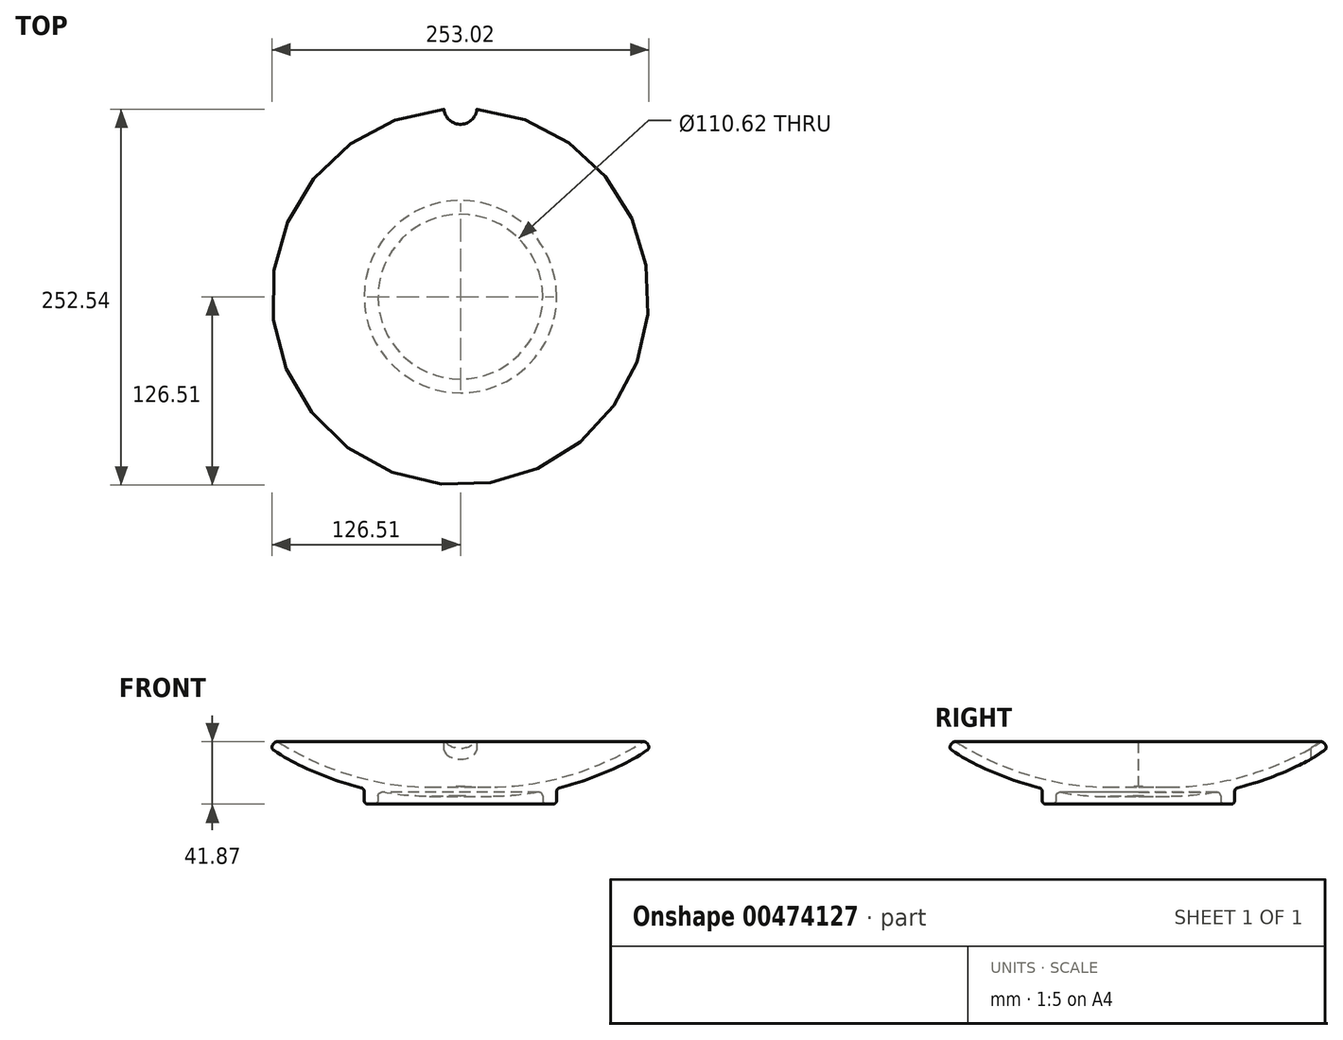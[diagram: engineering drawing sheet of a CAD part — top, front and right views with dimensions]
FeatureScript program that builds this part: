
annotation { "Feature Type Name" : "Feature", "Feature Type Description" : "" }
export const myFeature = defineFeature(function(context is Context, id is Id, definition is map)
    precondition{}
    {
        {
            var Q0;
            Q0=qCreatedBy(makeId("Front.planeOp"),FACE);
            var sketch = newSketch(context, id + "F0", { "sketchPlane" : qUnion([Q0])});
            skLineSegment(sketch, "E0", {"start": v(0, 0) * mm, "end": v(0, 6.35) * mm});
            skFitSpline(sketch, "E1", {"points": [v(0, 6.35) * mm, v(29.25, 6.35) * mm, v(74.57, 14.45) * mm, v(112.06, 30.1) * mm, v(124, 37.52) * mm], "startDerivative": vector(113.32, 2.1) * mm, "endDerivative": vector(60.26, 39.39) * mm});
            skFitSpline(sketch, "E2.0", {"points": [v(0.12, 0) * mm, v(2.37, 0.04) * mm, v(6.96, 0.02) * mm, v(13.03, -0.13) * mm, v(18.15, -0.2) * mm, v(22.14, -0.21) * mm, v(25.6, -0.15) * mm, v(28.45, -0.05) * mm, v(31.37, 0.1) * mm, v(35.1, 0.36) * mm, v(41.26, 0.95) * mm, v(49.22, 2.02) * mm, v(57.42, 3.53) * mm, v(64.05, 5.01) * mm, v(69.04, 6.26) * mm, v(74.03, 7.64) * mm, v(79, 9.16) * mm, v(83.89, 10.8) * mm, v(90.26, 13.12) * mm, v(97.88, 16.18) * mm, v(104.8, 19.3) * mm, v(109.78, 21.73) * mm, v(113.21, 23.5) * mm, v(116.3, 25.19) * mm, v(119.04, 26.78) * mm, v(121.46, 28.27) * mm, v(123.65, 29.68) * mm, v(125.64, 31) * mm, v(126.88, 31.81) * mm, v(127.48, 32.2) * mm]});
            skLineSegment(sketch, "E3", {"start": v(124, 37.52) * mm, "end": v(127.48, 32.2) * mm});
            skLineSegment(sketch, "E4", {"start": v(0, 0) * mm, "end": v(0.23, 0) * mm});
            skSolve(sketch);
        }
        {
            var Q0;
            Q0=makeQuery(id+"F0.imprint","IMPRINT",FACE,{"disambiguationData":[TD([[makeQuery(id+"F0.imprint","IMPRINT",EDGE,{"derivedFrom":sQuery(id+"F0.wireOp",EDGE,"E0")}),-1.0]])]});
            var Q1;
            Q1=sQuery(id+"F0.wireOp",EDGE,"E0");
            revolve(context, id + "F1", {"entities" : qUnion([Q0]), "axis" : qUnion([Q1]), "revolveType" : RevolveType.FULL});
        }
        {
            var Q0;
            Q0=qCreatedBy(makeId("Top.planeOp"),FACE);
            var sketch = newSketch(context, id + "F2", { "sketchPlane" : qUnion([Q0])});
            skCircle(sketch, "E5", {"center": v(0, 126.96) * mm, "radius": 11.13 * mm});
            skSolve(sketch);
        }
        {
            var Q0;
            Q0=makeQuery(id+"F2.imprint","IMPRINT",FACE,{"disambiguationData":[TD([[makeQuery(id+"F2.imprint","IMPRINT",EDGE,{"derivedFrom":sQuery(id+"F2.wireOp",EDGE,"E5")}),1.0]])]});
            extrude(context, id + "F3", {"entities" : qUnion([Q0]), "operationType" : NewBodyOperationType.REMOVE, "depth" : 87.88 * mm});
        }
        {
            var Q0;
            Q0=qCreatedBy(makeId("Top.planeOp"),FACE);
            var sketch = newSketch(context, id + "F4", { "sketchPlane" : qUnion([Q0])});
            skCircle(sketch, "E6", {"center": v(0, 0) * mm, "radius": 64.66 * mm});
            skCircle(sketch, "E7", {"center": v(0, 0) * mm, "radius": 55.31 * mm});
            skSolve(sketch);
        }
        {
            var Q0;
            Q0 = qSketchRegion(id + "F4", true);
            extrude(context, id + "F5", {"entities" : qUnion([Q0]), "operationType" : NewBodyOperationType.ADD, "endBound" : BoundingType.SYMMETRIC, "depth" : 10.67 * mm});
        }
        {
            var Q0;
            Q0=makeQuery(id+"F5.opExtrude","CAP_EDGE",EDGE,{"disambiguationData":[OSD([sQuery(id+"F4.wireOp",EDGE,"E6")])],"isStart":true});
            var Q1;
            Q1=makeQuery(id+"F5.boolean.opBoolean","INTERSECT",EDGE,{"derivedFrom":[makeQuery(id+"F1.opRevolve","SWEPT_FACE",FACE,{"disambiguationData":[OSD([sQuery(id+"F0.wireOp",EDGE,"E2.0")])]}),makeQuery(id+"F5.opExtrude","SWEPT_FACE",FACE,{"disambiguationData":[OSD([sQuery(id+"F4.wireOp",EDGE,"E6")])]})]});
            var Q2;
            Q2=makeQuery(id+"F5.opExtrude","CAP_EDGE",EDGE,{"disambiguationData":[OSD([sQuery(id+"F4.wireOp",EDGE,"E7")])],"isStart":true});
            var Q3;
            Q3=makeQuery(id+"F5.boolean.opBoolean","INTERSECT",EDGE,{"derivedFrom":[makeQuery(id+"F1.opRevolve","SWEPT_FACE",FACE,{"disambiguationData":[OSD([sQuery(id+"F0.wireOp",EDGE,"E2.0")])]}),makeQuery(id+"F5.opExtrude","SWEPT_FACE",FACE,{"disambiguationData":[OSD([sQuery(id+"F4.wireOp",EDGE,"E7")])]})]});
            var Q4;
            Q4=makeQuery(id+"F1.opRevolve","SWEPT_EDGE",EDGE,{"disambiguationData":[OSD([sQuery(id+"F0.wireOp",EDGE,"E2.0"),sQuery(id+"F0.wireOp",EDGE,"E3")])]});
            var Q5;
            Q5=makeQuery(id+"F1.opRevolve","SWEPT_EDGE",EDGE,{"disambiguationData":[OSD([sQuery(id+"F0.wireOp",EDGE,"E1"),sQuery(id+"F0.wireOp",EDGE,"E3")])]});
            fillet(context, id + "F6", {"entities" : qUnion([Q0, Q1, Q2, Q3, Q4, Q5]), "radius" : 2.54 * mm, "tangentPropagation" : true, "allowEdgeOverflow" : false});
        }
    });
